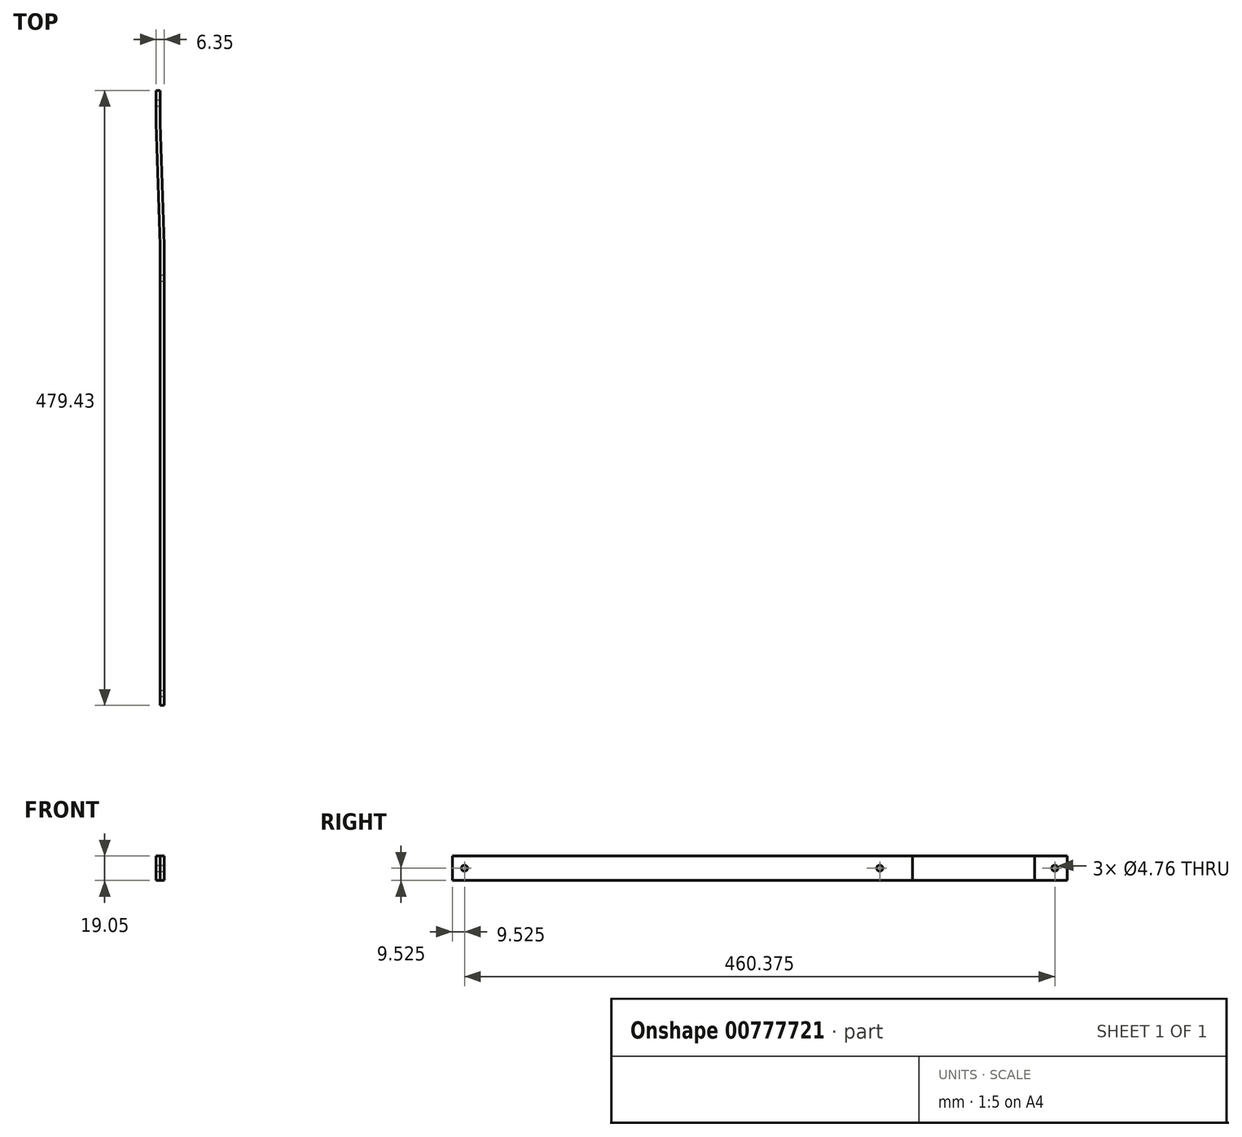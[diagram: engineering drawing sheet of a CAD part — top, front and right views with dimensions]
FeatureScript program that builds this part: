
annotation { "Feature Type Name" : "Feature", "Feature Type Description" : "" }
export const myFeature = defineFeature(function(context is Context, id is Id, definition is map)
    precondition{}
    {
        {
            var Q0;
            Q0=qCreatedBy(makeId("Top.planeOp"),FACE);
            var sketch = newSketch(context, id + "F0", { "sketchPlane" : qUnion([Q0])});
            skLineSegment(sketch, "E0", {"start": v(0, 0) * mm, "end": v(0, 358.78) * mm});
            skLineSegment(sketch, "E1", {"start": v(0, 358.77) * mm, "end": v(-3.18, 454.03) * mm});
            skLineSegment(sketch, "E2", {"start": v(-3.18, 454.03) * mm, "end": v(-3.18, 479.43) * mm});
            skLineSegment(sketch, "E3.0.left", {"start": v(-1.59, 0) * mm, "end": v(-1.59, 358.75) * mm});
            skLineSegment(sketch, "E3.0.right", {"start": v(1.59, 0) * mm, "end": v(1.59, 358.8) * mm});
            skLineSegment(sketch, "E3.1.left", {"start": v(-1.59, 358.75) * mm, "end": v(-4.76, 454) * mm});
            skLineSegment(sketch, "E3.1.right", {"start": v(1.59, 358.8) * mm, "end": v(-1.59, 454.05) * mm});
            skLineSegment(sketch, "E3.2.left", {"start": v(-4.76, 454) * mm, "end": v(-4.76, 479.43) * mm});
            skLineSegment(sketch, "E3.2.right", {"start": v(-1.59, 454.05) * mm, "end": v(-1.59, 479.43) * mm});
            skLineSegment(sketch, "E4", {"start": v(-4.76, 479.43) * mm, "end": v(-1.59, 479.43) * mm});
            skLineSegment(sketch, "E5", {"start": v(-1.59, 0) * mm, "end": v(1.59, 0) * mm});
            skSolve(sketch);
        }
        {
            var Q0;
            Q0 = qSketchRegion(id + "F0", true);
            extrude(context, id + "F1", {"entities" : qUnion([Q0]), "depth" : 19.05 * mm, "offsetDistance" : 25.4 * mm});
        }
        {
            var Q0;
            Q0=makeQuery(id+"F1.opExtrude","SWEPT_FACE",FACE,{"disambiguationData":[OSD([sQuery(id+"F0.wireOp",EDGE,"E3.0.right")])]});
            var sketch = newSketch(context, id + "F2", { "sketchPlane" : qUnion([Q0])});
            skCircle(sketch, "E6", {"center": v(9.53, 9.53) * mm, "radius": 2.38 * mm});
            skCircle(sketch, "E7", {"center": v(469.9, 9.53) * mm, "radius": 2.38 * mm});
            skCircle(sketch, "E8", {"center": v(333.38, 9.53) * mm, "radius": 2.38 * mm});
            skSolve(sketch);
        }
        {
            var Q0;
            Q0 = qSketchRegion(id + "F2", true);
            extrude(context, id + "F3", {"entities" : qUnion([Q0]), "operationType" : NewBodyOperationType.REMOVE, "oppositeDirection" : true, "depth" : 6.35 * mm, "offsetDistance" : 25.4 * mm});
        }
    });
